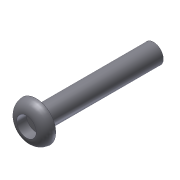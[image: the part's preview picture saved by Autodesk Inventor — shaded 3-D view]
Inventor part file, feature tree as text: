
AUTODESK INVENTOR PART (.ipt)
format: ipt  version: 2012 (Build 160160000, 160)  size: 92,672 bytes
history: native  units: in
note: dims shown in document units (in); Inventor stores cm internally (conversion verified against a paired STEP export)
features: extrude x2, sketch x2, fillet x1
ambient origin geometry x8: Origin, YZ Plane, XZ Plane, XY Plane, X Axis, Y Axis, Z Axis, Center Point
bodies: Solid1 (feature_tree)
feature tree (5):
  extrude  "Extrusion1"  Depth=1.5in TaperAngle=0.0deg
  extrude  "Extrusion2"  Depth=0.125in TaperAngle=0.0deg
  fillet  "Fillet1"  Radius=0.125in
  sketch  "Sketch1"  dims[d0=0.25in d1=1.5in d2=0.0in]
  sketch  "Sketch2"  dims[d3=0.5in d4=0.125in d5=0.0in d6=0.125in]
